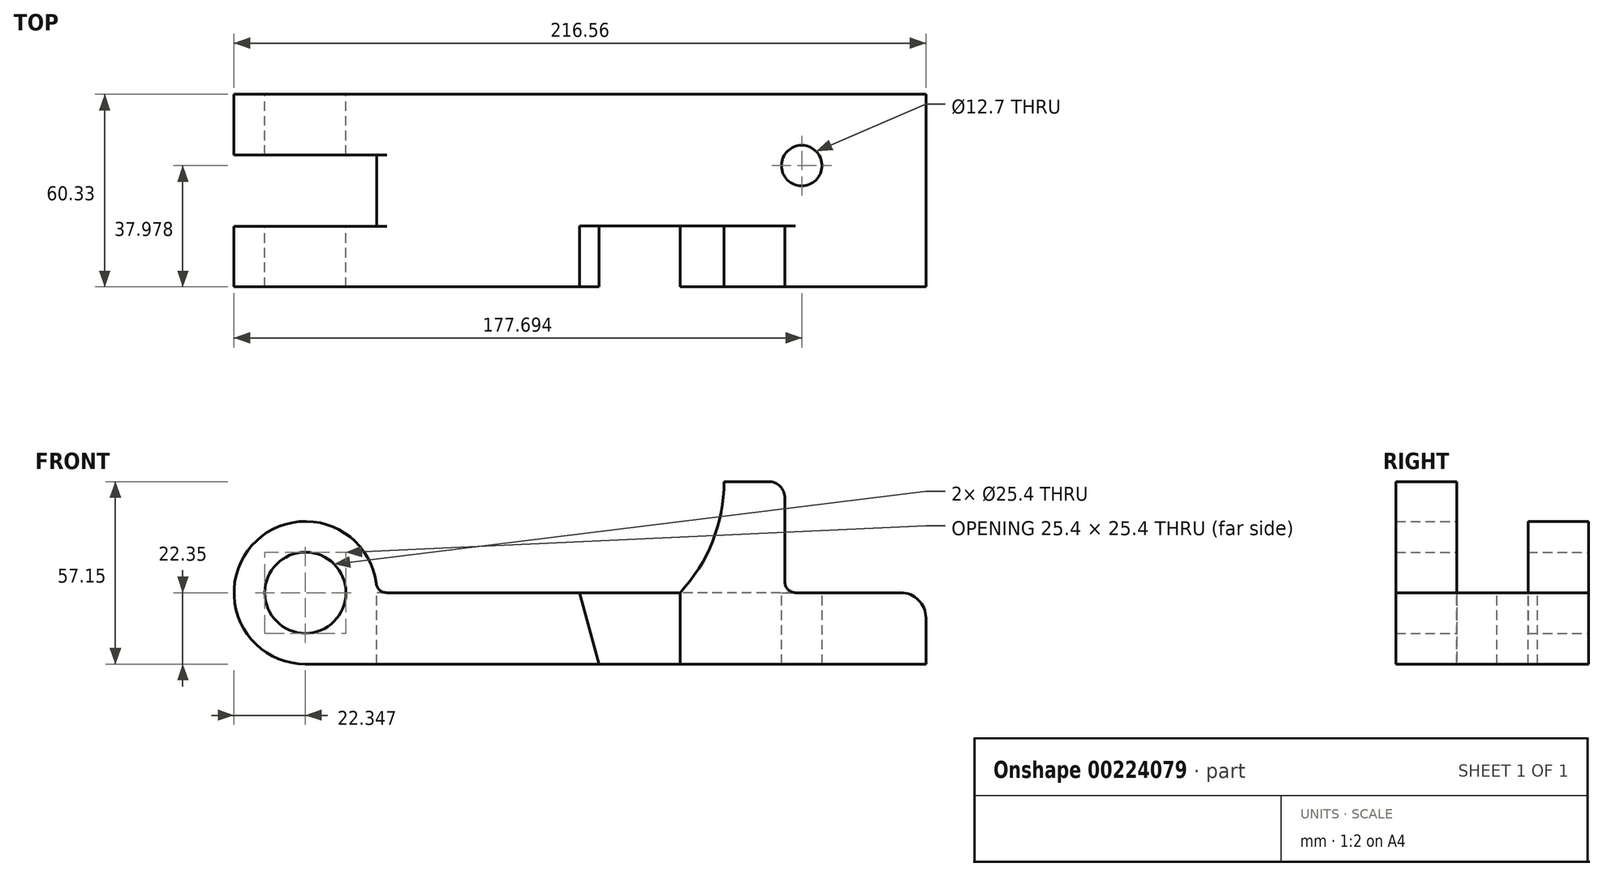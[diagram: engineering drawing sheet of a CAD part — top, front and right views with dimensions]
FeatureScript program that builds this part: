
annotation { "Feature Type Name" : "Feature", "Feature Type Description" : "" }
export const myFeature = defineFeature(function(context is Context, id is Id, definition is map)
    precondition{}
    {
        {
            var Q0;
            Q0=qCreatedBy(makeId("Front.planeOp"),FACE);
            var sketch = newSketch(context, id + "F0", { "sketchPlane" : qUnion([Q0])});
            skLineSegment(sketch, "E0", {"start": v(-165.4, 0) * mm, "end": v(138.42, 0) * mm, "construction": true});
            skCircle(sketch, "E1", {"center": v(-77.86, 0) * mm, "radius": 22.35 * mm});
            skCircle(sketch, "E2", {"center": v(-77.86, 0) * mm, "radius": 12.7 * mm});
            skLineSegment(sketch, "E3", {"start": v(-77.86, -22.35) * mm, "end": v(116.35, -22.35) * mm});
            skLineSegment(sketch, "E4", {"start": v(116.35, -22.35) * mm, "end": v(116.35, 0) * mm});
            skLineSegment(sketch, "E5", {"start": v(116.35, 0) * mm, "end": v(72.23, 0) * mm});
            skLineSegment(sketch, "E6", {"start": v(72.23, 0) * mm, "end": v(72.23, 34.8) * mm});
            skLineSegment(sketch, "E7", {"start": v(72.23, 34.8) * mm, "end": v(53.18, 34.8) * mm});
            skArc(sketch, "E8", {"start": v(39.38, 0) * mm, "mid": v(49.6, 16.08) * mm, "end": v(53.18, 34.8) * mm});
            skLineSegment(sketch, "E9.trimOffspring", {"start": v(39.38, 0) * mm, "end": v(-55.51, 0) * mm});
            skSolve(sketch);
        }
        {
            var Q0;
            Q0 = qSketchRegion(id + "F0", true);
            extrude(context, id + "F1", {"entities" : qUnion([Q0]), "depth" : 60.32 * mm});
        }
        {
            var Q0;
            Q0=makeQuery(id+"F1.opExtrude","CAP_FACE",FACE,{"disambiguationData":[OSD([sQuery(id+"F0.wireOp",EDGE,"E1"),sQuery(id+"F0.wireOp",EDGE,"E2"),sQuery(id+"F0.wireOp",EDGE,"E3"),sQuery(id+"F0.wireOp",EDGE,"E4"),sQuery(id+"F0.wireOp",EDGE,"E5"),sQuery(id+"F0.wireOp",EDGE,"E6"),sQuery(id+"F0.wireOp",EDGE,"E7"),sQuery(id+"F0.wireOp",EDGE,"E8"),sQuery(id+"F0.wireOp",EDGE,"E9.trimOffspring")])],"isStart":false});
            var sketch = newSketch(context, id + "F2", { "sketchPlane" : qUnion([Q0])});
            skLineSegment(sketch, "E10", {"start": v(39.38, 0) * mm, "end": v(39.38, -22.35) * mm});
            skLineSegment(sketch, "E11", {"start": v(39.38, 0) * mm, "end": v(7.99, 0) * mm});
            skLineSegment(sketch, "E12", {"start": v(7.99, 0) * mm, "end": v(13.98, -22.35) * mm});
            skLineSegment(sketch, "E13", {"start": v(13.98, -22.35) * mm, "end": v(39.38, -22.35) * mm});
            skLineSegment(sketch, "E14", {"start": v(-77.86, -22.35) * mm, "end": v(13.98, -22.35) * mm});
            skSolve(sketch);
        }
        {
            var Q0;
            Q0=makeQuery(id+"F2.imprint","IMPRINT",FACE,{"disambiguationData":[TD([[makeQuery(id+"F2.imprint","IMPRINT",EDGE,{"derivedFrom":sQuery(id+"F2.wireOp",EDGE,"E10")}),-1.0]])]});
            extrude(context, id + "F3", {"entities" : qUnion([Q0]), "operationType" : NewBodyOperationType.REMOVE, "oppositeDirection" : true, "depth" : 19.05 * mm});
        }
        {
            var Q0;
            Q0=makeQuery(id+"F1.opExtrude","SWEPT_FACE",FACE,{"disambiguationData":[OSD([sQuery(id+"F0.wireOp",EDGE,"E7")])]});
            var sketch = newSketch(context, id + "F4", { "sketchPlane" : qUnion([Q0])});
            skLineSegment(sketch, "E15.bottom", {"start": v(72.23, 0) * mm, "end": v(39.38, 0) * mm});
            skLineSegment(sketch, "E15.top", {"start": v(72.23, -41.28) * mm, "end": v(39.38, -41.28) * mm});
            skLineSegment(sketch, "E15.left", {"start": v(72.23, 0) * mm, "end": v(72.23, -41.28) * mm});
            skLineSegment(sketch, "E15.right", {"start": v(39.38, 0) * mm, "end": v(39.38, -41.28) * mm});
            skSolve(sketch);
        }
        {
            var Q0;
            Q0 = qSketchRegion(id + "F4", true);
            extrude(context, id + "F5", {"entities" : qUnion([Q0]), "operationType" : NewBodyOperationType.REMOVE, "oppositeDirection" : true, "depth" : 34.8 * mm});
        }
        {
            var Q0;
            Q0=makeQuery(id+"F5.boolean.opBoolean","MERGE",FACE,{"derivedFrom":[makeQuery(id+"F1.opExtrude","SWEPT_FACE",FACE,{"disambiguationData":[OSD([sQuery(id+"F0.wireOp",EDGE,"E5")])]}),makeQuery(id+"F1.opExtrude","SWEPT_FACE",FACE,{"disambiguationData":[OSD([sQuery(id+"F0.wireOp",EDGE,"E9.trimOffspring")])]}),makeQuery(id+"F5.opExtrude","CAP_FACE",FACE,{"disambiguationData":[OSD([sQuery(id+"F4.wireOp",EDGE,"E15.bottom"),sQuery(id+"F4.wireOp",EDGE,"E15.top"),sQuery(id+"F4.wireOp",EDGE,"E15.left"),sQuery(id+"F4.wireOp",EDGE,"E15.right")])],"isStart":false})]});
            cPlane(context, id + "F6", {"entities" : qUnion([Q0]), "cplaneType" : CPlaneType.OFFSET, "offset" : 22.35 * mm, "width" : 152.4 * mm, "height" : 152.4 * mm});
        }
        {
            var Q0;
            Q0=qCreatedBy(id+"F6.planeOp",FACE);
            var sketch = newSketch(context, id + "F7", { "sketchPlane" : qUnion([Q0])});
            skCircle(sketch, "E16", {"center": v(77.48, -22.35) * mm, "radius": 6.35 * mm});
            skLineSegment(sketch, "E17.bottom", {"start": v(-55.51, -19) * mm, "end": v(-100.4, -19) * mm});
            skLineSegment(sketch, "E17.top", {"start": v(-55.51, -41.33) * mm, "end": v(-100.4, -41.33) * mm});
            skLineSegment(sketch, "E17.left", {"start": v(-55.51, -19) * mm, "end": v(-55.51, -41.33) * mm});
            skLineSegment(sketch, "E17.right", {"start": v(-100.4, -19) * mm, "end": v(-100.4, -41.33) * mm});
            skSolve(sketch);
        }
        {
            var Q0;
            Q0=makeQuery(id+"F7.imprint","IMPRINT",FACE,{"disambiguationData":[TD([[makeQuery(id+"F7.imprint","IMPRINT",EDGE,{"derivedFrom":sQuery(id+"F7.wireOp",EDGE,"E17.bottom")}),1.0]])]});
            var Q1;
            Q1=makeQuery(id+"F7.imprint","IMPRINT",FACE,{"disambiguationData":[TD([[makeQuery(id+"F7.imprint","IMPRINT",EDGE,{"derivedFrom":sQuery(id+"F7.wireOp",EDGE,"E16")}),1.0]])]});
            extrude(context, id + "F8", {"entities" : qUnion([Q0, Q1]), "operationType" : NewBodyOperationType.REMOVE, "oppositeDirection" : true, "depth" : 44.7 * mm});
        }
        {
            var Q0;
            {var subQ0=sQuery(id+"F0.wireOp",EDGE,"E9.trimOffspring");var subQ1=sQuery(id+"F0.wireOp",EDGE,"E5");var subQ2=sQuery(id+"F0.wireOp",EDGE,"E1");Q0=makeQuery(id+"F8.boolean.opBoolean","SPLIT",EDGE,{"disambiguationData":[TD([makeQuery(id+"F1.opExtrude","SWEPT_FACE",FACE,{"disambiguationData":[OSD([subQ2])]}),makeQuery(id+"F1.opExtrude","CAP_FACE",FACE,{"disambiguationData":[OSD([subQ2,sQuery(id+"F0.wireOp",EDGE,"E2"),sQuery(id+"F0.wireOp",EDGE,"E3"),sQuery(id+"F0.wireOp",EDGE,"E4"),subQ1,sQuery(id+"F0.wireOp",EDGE,"E6"),sQuery(id+"F0.wireOp",EDGE,"E7"),sQuery(id+"F0.wireOp",EDGE,"E8"),subQ0])],"isStart":false}),makeQuery(id+"F1.opExtrude","SWEPT_FACE",FACE,{"disambiguationData":[OSD([subQ1])]}),makeQuery(id+"F1.opExtrude","SWEPT_FACE",FACE,{"disambiguationData":[OSD([subQ0])]}),makeQuery(id+"F5.opExtrude","CAP_FACE",FACE,{"disambiguationData":[OSD([sQuery(id+"F4.wireOp",EDGE,"E15.bottom"),sQuery(id+"F4.wireOp",EDGE,"E15.top"),sQuery(id+"F4.wireOp",EDGE,"E15.left"),sQuery(id+"F4.wireOp",EDGE,"E15.right")])],"isStart":false}),makeQuery(id+"F8.opExtrude","SWEPT_FACE",FACE,{"disambiguationData":[OSD([sQuery(id+"F7.wireOp",EDGE,"E17.top")])]}),makeQuery(id+"F8.opExtrude","SWEPT_FACE",FACE,{"disambiguationData":[OSD([sQuery(id+"F7.wireOp",EDGE,"E17.left")])]})])],"derivedFrom":makeQuery(id+"F1.opExtrude","SWEPT_EDGE",EDGE,{"disambiguationData":[OSD([subQ2,subQ0])]})});}
            var Q1;
            {var subQ0=sQuery(id+"F0.wireOp",EDGE,"E9.trimOffspring");var subQ1=sQuery(id+"F0.wireOp",EDGE,"E5");var subQ2=sQuery(id+"F0.wireOp",EDGE,"E1");Q1=makeQuery(id+"F8.boolean.opBoolean","SPLIT",EDGE,{"disambiguationData":[TD([makeQuery(id+"F1.opExtrude","SWEPT_FACE",FACE,{"disambiguationData":[OSD([subQ2])]}),makeQuery(id+"F1.opExtrude","CAP_FACE",FACE,{"disambiguationData":[OSD([subQ2,sQuery(id+"F0.wireOp",EDGE,"E2"),sQuery(id+"F0.wireOp",EDGE,"E3"),sQuery(id+"F0.wireOp",EDGE,"E4"),subQ1,sQuery(id+"F0.wireOp",EDGE,"E6"),sQuery(id+"F0.wireOp",EDGE,"E7"),sQuery(id+"F0.wireOp",EDGE,"E8"),subQ0])],"isStart":true}),makeQuery(id+"F1.opExtrude","SWEPT_FACE",FACE,{"disambiguationData":[OSD([subQ1])]}),makeQuery(id+"F1.opExtrude","SWEPT_FACE",FACE,{"disambiguationData":[OSD([subQ0])]}),makeQuery(id+"F5.opExtrude","CAP_FACE",FACE,{"disambiguationData":[OSD([sQuery(id+"F4.wireOp",EDGE,"E15.bottom"),sQuery(id+"F4.wireOp",EDGE,"E15.top"),sQuery(id+"F4.wireOp",EDGE,"E15.left"),sQuery(id+"F4.wireOp",EDGE,"E15.right")])],"isStart":false}),makeQuery(id+"F8.opExtrude","SWEPT_FACE",FACE,{"disambiguationData":[OSD([sQuery(id+"F7.wireOp",EDGE,"E17.bottom")])]}),makeQuery(id+"F8.opExtrude","SWEPT_FACE",FACE,{"disambiguationData":[OSD([sQuery(id+"F7.wireOp",EDGE,"E17.left")])]})])],"derivedFrom":makeQuery(id+"F1.opExtrude","SWEPT_EDGE",EDGE,{"disambiguationData":[OSD([subQ2,subQ0])]})});}
            fillet(context, id + "F9", {"entities" : qUnion([Q0, Q1]), "radius" : 3.3 * mm, "tangentPropagation" : true, "allowEdgeOverflow" : false});
        }
        {
            var Q0;
            Q0=makeQuery(id+"F1.opExtrude","SWEPT_EDGE",EDGE,{"disambiguationData":[OSD([sQuery(id+"F0.wireOp",EDGE,"E4"),sQuery(id+"F0.wireOp",EDGE,"E5")])]});
            fillet(context, id + "F10", {"entities" : qUnion([Q0]), "radius" : 7.87 * mm, "tangentPropagation" : true, "allowEdgeOverflow" : false});
        }
        {
            var Q0;
            Q0=makeQuery(id+"F1.opExtrude","SWEPT_EDGE",EDGE,{"disambiguationData":[OSD([sQuery(id+"F0.wireOp",EDGE,"E6"),sQuery(id+"F0.wireOp",EDGE,"E7")])]});
            fillet(context, id + "F11", {"entities" : qUnion([Q0]), "radius" : 5.08 * mm, "tangentPropagation" : true, "allowEdgeOverflow" : false});
        }
        {
            var Q0;
            Q0=makeQuery(id+"F1.opExtrude","SWEPT_EDGE",EDGE,{"disambiguationData":[OSD([sQuery(id+"F0.wireOp",EDGE,"E5"),sQuery(id+"F0.wireOp",EDGE,"E6")])]});
            fillet(context, id + "F12", {"entities" : qUnion([Q0]), "radius" : 3.3 * mm, "tangentPropagation" : true, "allowEdgeOverflow" : false});
        }
    });
